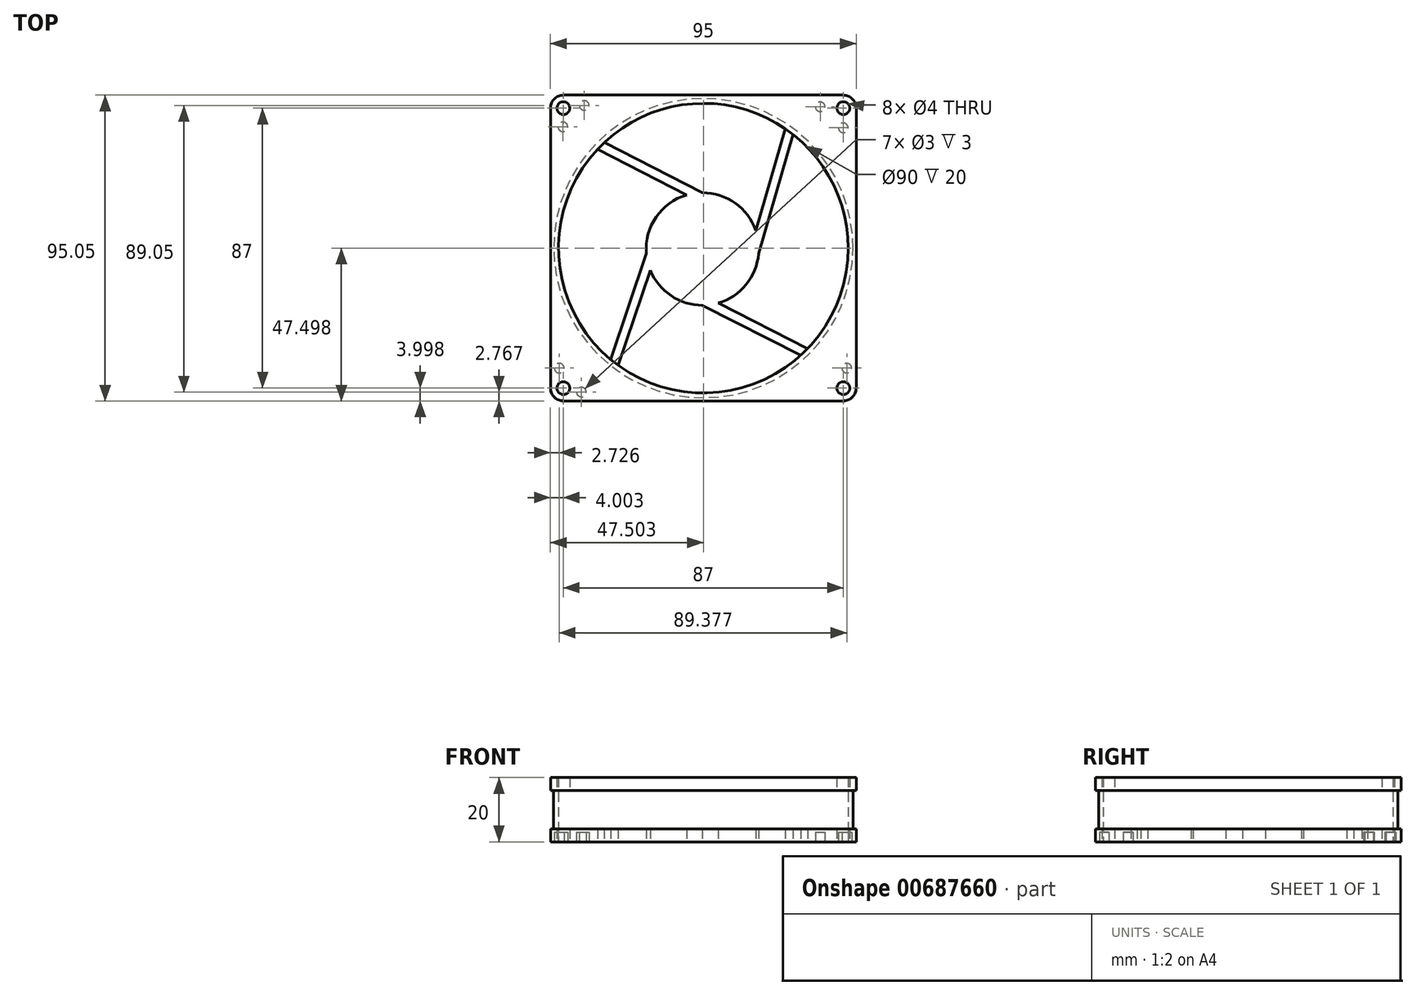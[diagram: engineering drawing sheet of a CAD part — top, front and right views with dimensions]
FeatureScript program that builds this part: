
annotation { "Feature Type Name" : "Feature", "Feature Type Description" : "" }
export const myFeature = defineFeature(function(context is Context, id is Id, definition is map)
    precondition{}
    {
        {
            var Q0;
            Q0=qCreatedBy(makeId("Top.planeOp"),FACE);
            var sketch = newSketch(context, id + "F0", { "sketchPlane" : qUnion([Q0])});
            skLineSegment(sketch, "E0", {"start": v(-59.2, 37.2) * mm, "end": v(27.8, 37.2) * mm});
            skLineSegment(sketch, "E1", {"start": v(31.8, 33.2) * mm, "end": v(31.8, -53.8) * mm});
            skLineSegment(sketch, "E2", {"start": v(27.8, -57.8) * mm, "end": v(-59.2, -57.8) * mm});
            skLineSegment(sketch, "E3", {"start": v(-63.2, -53.8) * mm, "end": v(-63.2, 33.2) * mm});
            skPoint(sketch, "E4.visualSharp", {"position": v(-63.2, 37.2) * mm});
            skArc(sketch, "E4.filletArc", {"start": v(-59.2, 37.2) * mm, "mid": v(-62.04, 36.04) * mm, "end": v(-63.2, 33.2) * mm});
            skPoint(sketch, "E5.visualSharp", {"position": v(31.8, 37.2) * mm});
            skArc(sketch, "E5.filletArc", {"start": v(31.8, 33.2) * mm, "mid": v(30.62, 36.04) * mm, "end": v(27.8, 37.2) * mm});
            skPoint(sketch, "E6.visualSharp", {"position": v(31.8, -57.8) * mm});
            skArc(sketch, "E6.filletArc", {"start": v(27.8, -57.8) * mm, "mid": v(30.62, -56.62) * mm, "end": v(31.8, -53.8) * mm});
            skPoint(sketch, "E7.visualSharp", {"position": v(-63.2, -57.8) * mm});
            skArc(sketch, "E7.filletArc", {"start": v(-63.2, -53.8) * mm, "mid": v(-62.04, -56.62) * mm, "end": v(-59.2, -57.8) * mm});
            skSolve(sketch);
        }
        {
            var Q0;
            Q0 = qSketchRegion(id + "F0", true);
            extrude(context, id + "F1", {"entities" : qUnion([Q0]), "depth" : 4 * mm, "offsetDistance" : 25 * mm});
        }
        {
            var Q0;
            Q0=makeQuery(id+"F1.opExtrude","CAP_FACE",FACE,{"disambiguationData":[OSD([sQuery(id+"F0.wireOp",EDGE,"E0"),sQuery(id+"F0.wireOp",EDGE,"E1"),sQuery(id+"F0.wireOp",EDGE,"E2"),sQuery(id+"F0.wireOp",EDGE,"E3"),sQuery(id+"F0.wireOp",EDGE,"E4.filletArc"),sQuery(id+"F0.wireOp",EDGE,"E5.filletArc"),sQuery(id+"F0.wireOp",EDGE,"E6.filletArc"),sQuery(id+"F0.wireOp",EDGE,"E7.filletArc")])],"isStart":false});
            var sketch = newSketch(context, id + "F2", { "sketchPlane" : qUnion([Q0])});
            skLineSegment(sketch, "E8", {"start": v(30.62, 36.04) * mm, "end": v(-62.04, -56.62) * mm});
            skLineSegment(sketch, "E9", {"start": v(-62.04, 36.04) * mm, "end": v(30.62, -56.62) * mm});
            skCircle(sketch, "E10", {"center": v(-15.7, -10.3) * mm, "radius": 46.5 * mm});
            skSolve(sketch);
        }
        {
            var Q0;
            Q0 = qSketchRegion(id + "F2", true);
            extrude(context, id + "F3", {"entities" : qUnion([Q0]), "operationType" : NewBodyOperationType.ADD, "depth" : 12 * mm, "offsetDistance" : 25 * mm});
        }
        {
            var Q0;
            Q0=makeQuery(id+"F1.opExtrude","CAP_FACE",FACE,{"disambiguationData":[OSD([sQuery(id+"F0.wireOp",EDGE,"E0"),sQuery(id+"F0.wireOp",EDGE,"E1"),sQuery(id+"F0.wireOp",EDGE,"E2"),sQuery(id+"F0.wireOp",EDGE,"E3"),sQuery(id+"F0.wireOp",EDGE,"E4.filletArc"),sQuery(id+"F0.wireOp",EDGE,"E5.filletArc"),sQuery(id+"F0.wireOp",EDGE,"E6.filletArc"),sQuery(id+"F0.wireOp",EDGE,"E7.filletArc")])],"isStart":true});
            var sketch = newSketch(context, id + "F4", { "sketchPlane" : qUnion([Q0])});
            skLineSegment(sketch, "E11", {"start": v(-62.04, 56.62) * mm, "end": v(30.62, -36.04) * mm});
            skLineSegment(sketch, "E12", {"start": v(30.62, 56.62) * mm, "end": v(-62.04, -36.04) * mm});
            skCircle(sketch, "E13", {"center": v(-15.7, 10.3) * mm, "radius": 45 * mm});
            skSolve(sketch);
        }
        {
            var Q0;
            Q0=qCreatedBy(makeId("Top.planeOp"),FACE);
            cPlane(context, id + "F5", {"entities" : qUnion([Q0]), "cplaneType" : CPlaneType.OFFSET, "offset" : 16 * mm, "width" : 150 * mm, "height" : 150 * mm});
        }
        {
            var Q0;
            Q0=qCreatedBy(id+"F5.planeOp",FACE);
            var sketch = newSketch(context, id + "F6", { "sketchPlane" : qUnion([Q0])});
            skLineSegment(sketch, "E14", {"start": v(-63.2, 33.26) * mm, "end": v(-63.2, -53.74) * mm});
            skLineSegment(sketch, "E15", {"start": v(-59.2, -57.74) * mm, "end": v(27.8, -57.74) * mm});
            skLineSegment(sketch, "E16", {"start": v(31.8, -53.74) * mm, "end": v(31.8, 33.26) * mm});
            skLineSegment(sketch, "E17", {"start": v(27.8, 37.26) * mm, "end": v(-59.2, 37.26) * mm});
            skPoint(sketch, "E18.visualSharp", {"position": v(-63.2, 37.26) * mm});
            skArc(sketch, "E18.filletArc", {"start": v(-59.2, 37.26) * mm, "mid": v(-62.04, 36.08) * mm, "end": v(-63.2, 33.26) * mm});
            skPoint(sketch, "E19.visualSharp", {"position": v(31.8, 37.26) * mm});
            skArc(sketch, "E19.filletArc", {"start": v(31.8, 33.26) * mm, "mid": v(30.62, 36.08) * mm, "end": v(27.8, 37.26) * mm});
            skPoint(sketch, "E20.visualSharp", {"position": v(31.8, -57.74) * mm});
            skArc(sketch, "E20.filletArc", {"start": v(27.8, -57.74) * mm, "mid": v(30.62, -56.57) * mm, "end": v(31.8, -53.74) * mm});
            skPoint(sketch, "E21.visualSharp", {"position": v(-63.2, -57.74) * mm});
            skArc(sketch, "E21.filletArc", {"start": v(-63.2, -53.74) * mm, "mid": v(-62.04, -56.57) * mm, "end": v(-59.2, -57.74) * mm});
            skSolve(sketch);
        }
        {
            var Q0;
            Q0 = qSketchRegion(id + "F6", true);
            extrude(context, id + "F7", {"entities" : qUnion([Q0]), "operationType" : NewBodyOperationType.ADD, "depth" : 4 * mm, "offsetDistance" : 25 * mm});
        }
        {
            var Q0;
            Q0 = qSketchRegion(id + "F4", true);
            extrude(context, id + "F8", {"entities" : qUnion([Q0]), "operationType" : NewBodyOperationType.REMOVE, "oppositeDirection" : true, "depth" : 25 * mm, "offsetDistance" : 25 * mm});
        }
        {
            var Q0;
            Q0=makeQuery(id+"F1.opExtrude","CAP_FACE",FACE,{"disambiguationData":[OSD([sQuery(id+"F0.wireOp",EDGE,"E0"),sQuery(id+"F0.wireOp",EDGE,"E1"),sQuery(id+"F0.wireOp",EDGE,"E2"),sQuery(id+"F0.wireOp",EDGE,"E3"),sQuery(id+"F0.wireOp",EDGE,"E4.filletArc"),sQuery(id+"F0.wireOp",EDGE,"E5.filletArc"),sQuery(id+"F0.wireOp",EDGE,"E6.filletArc"),sQuery(id+"F0.wireOp",EDGE,"E7.filletArc")])],"isStart":true});
            var sketch = newSketch(context, id + "F9", { "sketchPlane" : qUnion([Q0])});
            skCircle(sketch, "E22", {"center": v(27.8, 53.8) * mm, "radius": 2 * mm});
            skCircle(sketch, "E23", {"center": v(27.8, -33.2) * mm, "radius": 2 * mm});
            skCircle(sketch, "E24", {"center": v(-59.2, 53.8) * mm, "radius": 2 * mm});
            skCircle(sketch, "E25", {"center": v(-59.2, -33.2) * mm, "radius": 2 * mm});
            skSolve(sketch);
        }
        {
            var Q0;
            Q0 = qSketchRegion(id + "F9", true);
            extrude(context, id + "F10", {"entities" : qUnion([Q0]), "operationType" : NewBodyOperationType.REMOVE, "oppositeDirection" : true, "depth" : 25 * mm, "offsetDistance" : 25 * mm});
        }
        {
            var Q0;
            Q0=qCreatedBy(makeId("Top.planeOp"),FACE);
            var sketch = newSketch(context, id + "F11", { "sketchPlane" : qUnion([Q0])});
            skLineSegment(sketch, "E26", {"start": v(-3.6, -22.93) * mm, "end": v(-15.98, -10.56) * mm});
            skLineSegment(sketch, "E27", {"start": v(-28.35, 1.81) * mm, "end": v(-3.6, -22.93) * mm});
            skLineSegment(sketch, "E28", {"start": v(-28.34, -22.94) * mm, "end": v(-3.61, 1.82) * mm});
            skCircle(sketch, "E29", {"center": v(-15.98, -10.56) * mm, "radius": 17.5 * mm});
            skPoint(sketch, "E30.orphan", {"position": v(-63.45, -58.1) * mm});
            skPoint(sketch, "E31.orphan", {"position": v(-63.45, 36.9) * mm});
            skArc(sketch, "E32", {"start": v(15.47, -44.13) * mm, "mid": v(16.55, -43.08) * mm, "end": v(17.6, -42) * mm});
            skLineSegment(sketch, "E33", {"start": v(-15.98, -28.06) * mm, "end": v(15.47, -44.13) * mm});
            skLineSegment(sketch, "E34", {"start": v(15.47, -44.13) * mm, "end": v(-15.98, -28.06) * mm});
            skLineSegment(sketch, "E35", {"start": v(-15.98, 6.94) * mm, "end": v(-47.43, 23) * mm});
            skLineSegment(sketch, "E36", {"start": v(-47.43, 23) * mm, "end": v(-49.55, 20.89) * mm});
            skLineSegment(sketch, "E37", {"start": v(-49.55, 20.89) * mm, "end": v(-20.88, 6.24) * mm});
            skLineSegment(sketch, "E38", {"start": v(15.47, -44.13) * mm, "end": v(17.6, -42) * mm});
            skLineSegment(sketch, "E39", {"start": v(17.6, -42) * mm, "end": v(-11.08, -27.36) * mm});
            skLineSegment(sketch, "E40", {"start": v(1.46, -12) * mm, "end": v(12.34, 25.69) * mm});
            skLineSegment(sketch, "E41", {"start": v(12.34, 25.69) * mm, "end": v(9.92, 27.46) * mm});
            skLineSegment(sketch, "E42", {"start": v(9.92, 27.46) * mm, "end": v(0.58, -4.9) * mm});
            skLineSegment(sketch, "E43", {"start": v(-33.42, -12) * mm, "end": v(-45, -46.25) * mm});
            skLineSegment(sketch, "E44", {"start": v(-45, -46.25) * mm, "end": v(-42.61, -48.06) * mm});
            skLineSegment(sketch, "E45", {"start": v(-42.61, -48.06) * mm, "end": v(-32.17, -17.19) * mm});
            skArc(sketch, "E46.trimOffspring", {"start": v(-45, -46.25) * mm, "mid": v(-43.82, -47.17) * mm, "end": v(-42.61, -48.06) * mm});
            skArc(sketch, "E47.trimOffspring", {"start": v(-47.43, 23) * mm, "mid": v(-48.5, 21.96) * mm, "end": v(-49.55, 20.89) * mm});
            skArc(sketch, "E48.trimOffspring", {"start": v(12.34, 25.69) * mm, "mid": v(11.15, 26.6) * mm, "end": v(9.92, 27.46) * mm});
            skSolve(sketch);
        }
        {
            var Q0;
            Q0 = qSketchRegion(id + "F11", true);
            extrude(context, id + "F12", {"entities" : qUnion([Q0]), "operationType" : NewBodyOperationType.ADD, "depth" : 4 * mm, "offsetDistance" : 25 * mm});
        }
        {
            var Q0;
            Q0=makeQuery(id+"F12.boolean.opBoolean","MERGE",FACE,{"derivedFrom":[makeQuery(id+"F1.opExtrude","CAP_FACE",FACE,{"disambiguationData":[OSD([sQuery(id+"F0.wireOp",EDGE,"E0"),sQuery(id+"F0.wireOp",EDGE,"E1"),sQuery(id+"F0.wireOp",EDGE,"E2"),sQuery(id+"F0.wireOp",EDGE,"E3"),sQuery(id+"F0.wireOp",EDGE,"E4.filletArc"),sQuery(id+"F0.wireOp",EDGE,"E5.filletArc"),sQuery(id+"F0.wireOp",EDGE,"E6.filletArc"),sQuery(id+"F0.wireOp",EDGE,"E7.filletArc")])],"isStart":true}),makeQuery(id+"F12.opExtrude","CAP_FACE",FACE,{"disambiguationData":[OSD([sQuery(id+"F11.wireOp",EDGE,"E29"),sQuery(id+"F11.wireOp",EDGE,"E32"),sQuery(id+"F11.wireOp",EDGE,"E34"),sQuery(id+"F11.wireOp",EDGE,"E35"),sQuery(id+"F11.wireOp",EDGE,"E37"),sQuery(id+"F11.wireOp",EDGE,"E39"),sQuery(id+"F11.wireOp",EDGE,"E40"),sQuery(id+"F11.wireOp",EDGE,"E42"),sQuery(id+"F11.wireOp",EDGE,"E43"),sQuery(id+"F11.wireOp",EDGE,"E45"),sQuery(id+"F11.wireOp",EDGE,"E46.trimOffspring"),sQuery(id+"F11.wireOp",EDGE,"E47.trimOffspring"),sQuery(id+"F11.wireOp",EDGE,"E48.trimOffspring")])],"isStart":true})]});
            var sketch = newSketch(context, id + "F13", { "sketchPlane" : qUnion([Q0])});
            skCircle(sketch, "E49", {"center": v(28.9, 47.58) * mm, "radius": 1.5 * mm});
            skCircle(sketch, "E50", {"center": v(-53.6, 55.02) * mm, "radius": 1.5 * mm});
            skCircle(sketch, "E51", {"center": v(-60.48, 47.58) * mm, "radius": 1.5 * mm});
            skCircle(sketch, "E52", {"center": v(27.8, -27.1) * mm, "radius": 1.5 * mm});
            skCircle(sketch, "E53", {"center": v(-59.35, -27.41) * mm, "radius": 1.5 * mm});
            skCircle(sketch, "E54", {"center": v(-52.71, -34.03) * mm, "radius": 1.5 * mm});
            skCircle(sketch, "E55", {"center": v(20.6, -33.64) * mm, "radius": 1.5 * mm});
            skSolve(sketch);
        }
        {
            var Q0;
            Q0 = qSketchRegion(id + "F13", true);
            extrude(context, id + "F14", {"entities" : qUnion([Q0]), "operationType" : NewBodyOperationType.REMOVE, "oppositeDirection" : true, "depth" : 3 * mm, "offsetDistance" : 25 * mm});
        }
    });
